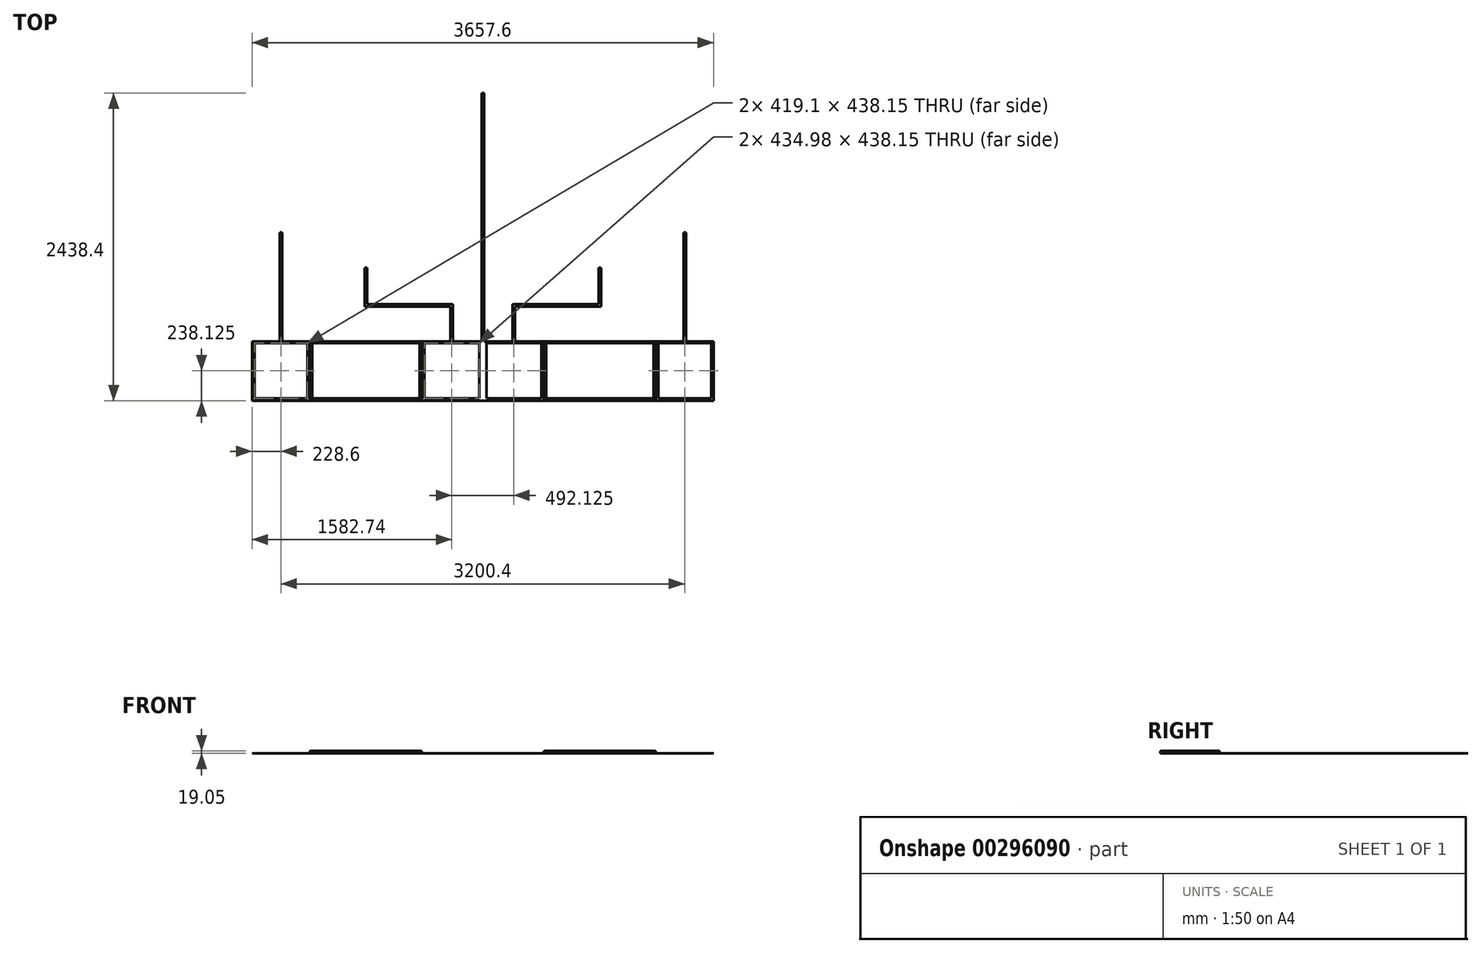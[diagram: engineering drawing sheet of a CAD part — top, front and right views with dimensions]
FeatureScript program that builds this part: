
annotation { "Feature Type Name" : "Feature", "Feature Type Description" : "" }
export const myFeature = defineFeature(function(context is Context, id is Id, definition is map)
    precondition{}
    {
        {
            var Q0;
            Q0=qCreatedBy(makeId("Top.planeOp"),FACE);
            var sketch = newSketch(context, id + "F0", { "sketchPlane" : qUnion([Q0])});
            skLineSegment(sketch, "E0.bottom", {"start": v(0, 1187.45) * mm, "end": v(-1828.8, 1187.45) * mm});
            skLineSegment(sketch, "E0.top", {"start": v(0, -1250.95) * mm, "end": v(-1828.8, -1250.95) * mm});
            skLineSegment(sketch, "E0.right", {"start": v(-1828.8, 1187.45) * mm, "end": v(-1828.8, -1250.95) * mm});
            skPoint(sketch, "E0.middle", {"position": v(0, 0) * mm});
            skLineSegment(sketch, "E1.bottom", {"start": v(0, 1187.45) * mm, "end": v(-9.52, 1187.45) * mm});
            skLineSegment(sketch, "E1.top", {"start": v(0, -1250.95) * mm, "end": v(-9.52, -1250.95) * mm});
            skLineSegment(sketch, "E1.right", {"start": v(-9.53, 1187.45) * mm, "end": v(-9.53, -1250.95) * mm});
            skPoint(sketch, "E2", {"position": v(-1828.8, -793.75) * mm});
            skLineSegment(sketch, "E3", {"start": v(-1809.75, -793.75) * mm, "end": v(-1590.67, -793.75) * mm});
            skPoint(sketch, "E4", {"position": v(-1809.75, -1250.95) * mm});
            skLineSegment(sketch, "E5", {"start": v(-1809.75, -1231.9) * mm, "end": v(-1809.75, -793.75) * mm});
            skPoint(sketch, "E6", {"position": v(-1371.6, -1250.95) * mm});
            skPoint(sketch, "E7", {"position": v(-1390.65, -1250.95) * mm});
            skLineSegment(sketch, "E8", {"start": v(-1371.6, -1250.95) * mm, "end": v(-1371.6, -793.75) * mm});
            skLineSegment(sketch, "E9", {"start": v(-1390.65, -1231.9) * mm, "end": v(-1390.65, -793.75) * mm});
            skLineSegment(sketch, "E10.trimOffspring", {"start": v(-1390.65, -781.05) * mm, "end": v(-1809.75, -781.05) * mm});
            skPoint(sketch, "E11", {"position": v(-1828.8, -1231.9) * mm});
            skLineSegment(sketch, "E12", {"start": v(-1809.75, -1231.9) * mm, "end": v(-1390.65, -1231.9) * mm});
            skPoint(sketch, "E13", {"position": v(-482.6, -1250.95) * mm});
            skPoint(sketch, "E14", {"position": v(-501.65, -1250.95) * mm});
            skPoint(sketch, "E15", {"position": v(-1352.55, -1250.95) * mm});
            skLineSegment(sketch, "E16", {"start": v(-1352.55, -1231.9) * mm, "end": v(-1352.55, -793.75) * mm});
            skLineSegment(sketch, "E17", {"start": v(-482.6, -1250.95) * mm, "end": v(-482.6, -781.05) * mm});
            skLineSegment(sketch, "E18", {"start": v(-482.6, -793.75) * mm, "end": v(-482.6, -781.05) * mm});
            skLineSegment(sketch, "E19", {"start": v(-501.65, -1231.9) * mm, "end": v(-501.65, -793.75) * mm});
            skLineSegment(sketch, "E20", {"start": v(-1352.55, -1231.9) * mm, "end": v(-501.65, -1231.9) * mm});
            skLineSegment(sketch, "E21.trimOffspring", {"start": v(-501.65, -781.05) * mm, "end": v(-1352.55, -781.05) * mm});
            skPoint(sketch, "E22", {"position": v(-463.55, -1250.95) * mm});
            skPoint(sketch, "E23", {"position": v(-28.57, -1250.95) * mm});
            skLineSegment(sketch, "E24", {"start": v(-463.55, -1231.9) * mm, "end": v(-463.55, -793.75) * mm});
            skLineSegment(sketch, "E25", {"start": v(-28.58, -1231.9) * mm, "end": v(-28.58, -793.75) * mm});
            skLineSegment(sketch, "E26", {"start": v(-463.55, -1231.9) * mm, "end": v(-28.57, -1231.9) * mm});
            skLineSegment(sketch, "E27.trimOffspring", {"start": v(-28.58, -781.05) * mm, "end": v(-463.55, -781.05) * mm});
            skPoint(sketch, "E28", {"position": v(-246.06, -793.75) * mm});
            skPoint(sketch, "E29", {"position": v(-9.52, -793.75) * mm});
            skPoint(sketch, "E30", {"position": v(-246.06, -628.65) * mm});
            skLineSegment(sketch, "E31.top", {"start": v(-236.54, -793.75) * mm, "end": v(-255.59, -793.75) * mm});
            skLineSegment(sketch, "E31.left", {"start": v(-236.54, -463.55) * mm, "end": v(-236.54, -781.05) * mm});
            skLineSegment(sketch, "E31.right", {"start": v(-255.59, -504.83) * mm, "end": v(-255.59, -781.05) * mm});
            skPoint(sketch, "E32", {"position": v(-927.1, -793.75) * mm});
            skLineSegment(sketch, "E33.bottom", {"start": v(-917.58, -485.78) * mm, "end": v(-236.54, -485.78) * mm});
            skLineSegment(sketch, "E33.top", {"start": v(-936.35, -504.83) * mm, "end": v(-255.59, -504.83) * mm});
            skPoint(sketch, "E33.middle", {"position": v(-586.44, -495.3) * mm});
            skPoint(sketch, "E34", {"position": v(-927.1, -350.84) * mm});
            skLineSegment(sketch, "E35.bottom", {"start": v(-917.58, -504.83) * mm, "end": v(-936.63, -504.83) * mm});
            skLineSegment(sketch, "E35.top", {"start": v(-917.58, -196.85) * mm, "end": v(-936.63, -196.85) * mm});
            skLineSegment(sketch, "E35.left", {"start": v(-917.58, -485.78) * mm, "end": v(-917.58, -196.85) * mm});
            skLineSegment(sketch, "E35.right", {"start": v(-936.63, -504.83) * mm, "end": v(-936.63, -196.85) * mm});
            skPoint(sketch, "E36.trimOffspring.end.orphan", {"position": v(-917.85, -196.85) * mm});
            skPoint(sketch, "E37", {"position": v(-1600.2, -793.75) * mm});
            skPoint(sketch, "E38", {"position": v(-1600.2, -355.6) * mm});
            skLineSegment(sketch, "E39.bottom", {"start": v(-1609.72, -793.75) * mm, "end": v(-1590.67, -793.75) * mm});
            skLineSegment(sketch, "E39.top", {"start": v(-1609.72, 82.55) * mm, "end": v(-1590.67, 82.55) * mm});
            skLineSegment(sketch, "E39.left", {"start": v(-1609.73, -781.05) * mm, "end": v(-1609.73, 82.55) * mm});
            skLineSegment(sketch, "E39.right", {"start": v(-1590.68, -781.05) * mm, "end": v(-1590.68, 82.55) * mm});
            skPoint(sketch, "E40.orphan", {"position": v(-1600.2, 82.55) * mm});
            skPoint(sketch, "E41", {"position": v(0, 1187.45) * mm});
            skLineSegment(sketch, "E42", {"start": v(0, 1187.45) * mm, "end": v(0, -1250.95) * mm});
            skLineSegment(sketch, "E43.MirrorCS", {"start": v(0, 1187.45) * mm, "end": v(9.52, 1187.45) * mm});
            skLineSegment(sketch, "E44.MirrorCS", {"start": v(0, -1250.95) * mm, "end": v(9.52, -1250.95) * mm});
            skLineSegment(sketch, "E45.MirrorCS", {"start": v(9.52, 1187.45) * mm, "end": v(9.53, -1250.95) * mm});
            skLineSegment(sketch, "E46.MirrorCS", {"start": v(-1809.75, -793.75) * mm, "end": v(-1390.65, -793.75) * mm});
            skLineSegment(sketch, "E47", {"start": v(-1809.75, -781.05) * mm, "end": v(-1828.8, -781.05) * mm});
            skLineSegment(sketch, "E48", {"start": v(-1390.65, -781.05) * mm, "end": v(-1352.55, -781.05) * mm});
            skLineSegment(sketch, "E49.trimOffspring", {"start": v(-1352.55, -793.75) * mm, "end": v(-501.65, -793.75) * mm});
            skLineSegment(sketch, "E50", {"start": v(-1371.6, -793.75) * mm, "end": v(-1371.6, -781.05) * mm});
            skLineSegment(sketch, "E51.trimOffspring", {"start": v(-1352.55, -793.75) * mm, "end": v(-927.1, -793.75) * mm});
            skLineSegment(sketch, "E52", {"start": v(-501.65, -781.05) * mm, "end": v(-463.55, -781.05) * mm});
            skLineSegment(sketch, "E53.trimOffspring", {"start": v(-463.55, -793.75) * mm, "end": v(-28.58, -793.75) * mm});
            skLineSegment(sketch, "E54", {"start": v(-28.58, -781.05) * mm, "end": v(-9.53, -781.05) * mm});
            skLineSegment(sketch, "E55.trimOffspring", {"start": v(-9.52, -793.75) * mm, "end": v(0, -793.75) * mm});
            skLineSegment(sketch, "E56.MirrorCS", {"start": v(0, 1187.45) * mm, "end": v(-9.53, 1187.45) * mm});
            skLineSegment(sketch, "E57.MirrorCS", {"start": v(9.52, -793.75) * mm, "end": v(0, -793.75) * mm});
            skLineSegment(sketch, "E58.MirrorCS", {"start": v(1809.75, -781.05) * mm, "end": v(1828.8, -781.05) * mm});
            skLineSegment(sketch, "E59.MirrorCS", {"start": v(28.57, -781.05) * mm, "end": v(9.52, -781.05) * mm});
            skLineSegment(sketch, "E60.MirrorCS", {"start": v(1371.6, -793.75) * mm, "end": v(1371.6, -781.05) * mm});
            skLineSegment(sketch, "E61.MirrorCS", {"start": v(482.6, -793.75) * mm, "end": v(482.6, -781.05) * mm});
            skLineSegment(sketch, "E62.MirrorCS", {"start": v(501.65, -781.05) * mm, "end": v(463.55, -781.05) * mm});
            skLineSegment(sketch, "E63.MirrorCS", {"start": v(1390.65, -781.05) * mm, "end": v(1352.55, -781.05) * mm});
            skLineSegment(sketch, "E64.MirrorCS", {"start": v(917.57, -504.83) * mm, "end": v(936.62, -504.83) * mm});
            skLineSegment(sketch, "E65.MirrorCS", {"start": v(1609.72, -793.75) * mm, "end": v(1590.67, -793.75) * mm});
            skLineSegment(sketch, "E66.MirrorCS", {"start": v(917.57, -196.85) * mm, "end": v(936.62, -196.85) * mm});
            skLineSegment(sketch, "E67.MirrorCS", {"start": v(236.54, -793.75) * mm, "end": v(255.59, -793.75) * mm});
            skLineSegment(sketch, "E68.MirrorCS", {"start": v(1609.72, 82.55) * mm, "end": v(1590.67, 82.55) * mm});
            skPoint(sketch, "E69.MirrorP", {"position": v(246.06, -628.65) * mm});
            skLineSegment(sketch, "E70.MirrorCS", {"start": v(28.57, -781.05) * mm, "end": v(463.55, -781.05) * mm});
            skLineSegment(sketch, "E71.MirrorCS", {"start": v(1352.55, -793.75) * mm, "end": v(927.1, -793.75) * mm});
            skLineSegment(sketch, "E72.MirrorCS", {"start": v(463.55, -793.75) * mm, "end": v(28.57, -793.75) * mm});
            skPoint(sketch, "E73.MirrorP", {"position": v(927.1, -350.84) * mm});
            skLineSegment(sketch, "E74.MirrorCS", {"start": v(0, -1250.95) * mm, "end": v(1828.8, -1250.95) * mm});
            skLineSegment(sketch, "E75.MirrorCS", {"start": v(0, 1187.45) * mm, "end": v(1828.8, 1187.45) * mm});
            skPoint(sketch, "E76.MirrorP", {"position": v(1600.2, -355.6) * mm});
            skLineSegment(sketch, "E77.MirrorCS", {"start": v(1371.6, -1250.95) * mm, "end": v(1371.6, -793.75) * mm});
            skPoint(sketch, "E78.MirrorP", {"position": v(9.52, -793.75) * mm});
            skLineSegment(sketch, "E79.MirrorCS", {"start": v(1809.75, -793.75) * mm, "end": v(1390.65, -793.75) * mm});
            skPoint(sketch, "E80.MirrorP", {"position": v(482.6, -1250.95) * mm});
            skLineSegment(sketch, "E81.MirrorCS", {"start": v(1809.75, -793.75) * mm, "end": v(1590.67, -793.75) * mm});
            skLineSegment(sketch, "E82.MirrorCS", {"start": v(501.65, -781.05) * mm, "end": v(1352.55, -781.05) * mm});
            skPoint(sketch, "E83.MirrorP", {"position": v(28.57, -1250.95) * mm});
            skPoint(sketch, "E84.MirrorP", {"position": v(1828.8, -793.75) * mm});
            skPoint(sketch, "E85.MirrorP", {"position": v(1371.6, -1250.95) * mm});
            skLineSegment(sketch, "E86.MirrorCS", {"start": v(1828.8, 1187.45) * mm, "end": v(1828.8, -1250.95) * mm});
            skLineSegment(sketch, "E87.MirrorCS", {"start": v(482.6, -1250.95) * mm, "end": v(482.6, -781.05) * mm});
            skLineSegment(sketch, "E88.MirrorCS", {"start": v(1590.67, -781.05) * mm, "end": v(1590.67, 82.55) * mm});
            skPoint(sketch, "E89.MirrorP", {"position": v(917.85, -196.85) * mm});
            skLineSegment(sketch, "E90.MirrorCS", {"start": v(255.59, -504.83) * mm, "end": v(255.59, -781.05) * mm});
            skLineSegment(sketch, "E91.MirrorCS", {"start": v(1352.55, -1231.9) * mm, "end": v(1352.55, -793.75) * mm});
            skLineSegment(sketch, "E92.MirrorCS", {"start": v(1352.55, -793.75) * mm, "end": v(501.65, -793.75) * mm});
            skPoint(sketch, "E93.MirrorP", {"position": v(1600.2, 82.55) * mm});
            skLineSegment(sketch, "E94.MirrorCS", {"start": v(1809.75, -1231.9) * mm, "end": v(1390.65, -1231.9) * mm});
            skLineSegment(sketch, "E95.MirrorCS", {"start": v(1390.65, -781.05) * mm, "end": v(1809.75, -781.05) * mm});
            skPoint(sketch, "E96.MirrorP", {"position": v(1828.8, -1231.9) * mm});
            skLineSegment(sketch, "E97.MirrorCS", {"start": v(936.62, -504.83) * mm, "end": v(936.62, -196.85) * mm});
            skLineSegment(sketch, "E98.MirrorCS", {"start": v(917.57, -485.78) * mm, "end": v(236.54, -485.78) * mm});
            skPoint(sketch, "E99.MirrorP", {"position": v(501.65, -1250.95) * mm});
            skPoint(sketch, "E100.MirrorP", {"position": v(1600.2, -793.75) * mm});
            skLineSegment(sketch, "E101.MirrorCS", {"start": v(917.57, -485.78) * mm, "end": v(917.57, -196.85) * mm});
            skLineSegment(sketch, "E102.MirrorCS", {"start": v(1809.75, -1231.9) * mm, "end": v(1809.75, -793.75) * mm});
            skLineSegment(sketch, "E103.MirrorCS", {"start": v(28.58, -1231.9) * mm, "end": v(28.57, -793.75) * mm});
            skPoint(sketch, "E104.MirrorP", {"position": v(586.44, -495.3) * mm});
            skPoint(sketch, "E105.MirrorP", {"position": v(1809.75, -1250.95) * mm});
            skLineSegment(sketch, "E106.MirrorCS", {"start": v(236.54, -463.55) * mm, "end": v(236.54, -781.05) * mm});
            skPoint(sketch, "E107.MirrorP", {"position": v(463.55, -1250.95) * mm});
            skPoint(sketch, "E108.MirrorP", {"position": v(1390.65, -1250.95) * mm});
            skLineSegment(sketch, "E109.MirrorCS", {"start": v(1390.65, -1231.9) * mm, "end": v(1390.65, -793.75) * mm});
            skPoint(sketch, "E110.MirrorP", {"position": v(246.06, -793.75) * mm});
            skPoint(sketch, "E111.MirrorP", {"position": v(1352.55, -1250.95) * mm});
            skPoint(sketch, "E112.MirrorP", {"position": v(927.1, -793.75) * mm});
            skLineSegment(sketch, "E113.MirrorCS", {"start": v(463.55, -1231.9) * mm, "end": v(28.57, -1231.9) * mm});
            skLineSegment(sketch, "E114.MirrorCS", {"start": v(501.65, -1231.9) * mm, "end": v(501.65, -793.75) * mm});
            skLineSegment(sketch, "E115.MirrorCS", {"start": v(936.35, -504.83) * mm, "end": v(255.59, -504.83) * mm});
            skLineSegment(sketch, "E116.MirrorCS", {"start": v(1352.55, -1231.9) * mm, "end": v(501.65, -1231.9) * mm});
            skLineSegment(sketch, "E117.MirrorCS", {"start": v(1609.72, -781.05) * mm, "end": v(1609.72, 82.55) * mm});
            skLineSegment(sketch, "E118.MirrorCS", {"start": v(463.55, -1231.9) * mm, "end": v(463.55, -793.75) * mm});
            skSolve(sketch);
        }
        {
            var Q0;
            Q0=makeQuery(id+"F0.imprint","IMPRINT",FACE,{"disambiguationData":[TD([[makeQuery(id+"F0.imprint","IMPRINT",EDGE,{"derivedFrom":sQuery(id+"F0.wireOp",EDGE,"E39.top")}),-1.0]])]});
            var Q1;
            Q1=makeQuery(id+"F0.imprint","IMPRINT",FACE,{"disambiguationData":[TD([[makeQuery(id+"F0.imprint","IMPRINT",EDGE,{"derivedFrom":sQuery(id+"F0.wireOp",EDGE,"E5")}),1.0]])]});
            var Q2;
            {var subQ4=sQuery(id+"F0.wireOp",EDGE,"E17");Q2=makeQuery(id+"F0.imprint","IMPRINT",FACE,{"disambiguationData":[TD([[makeQuery(id+"F0.imprint","IMPRINT",EDGE,{"derivedFrom":subQ4}),-1.0]])]});}
            var Q3;
            {var subQ2=sQuery(id+"F0.wireOp",EDGE,"E31.left");Q3=makeQuery(id+"F0.imprint","IMPRINT",FACE,{"disambiguationData":[TD([[makeQuery(id+"F0.imprint","IMPRINT",EDGE,{"derivedFrom":subQ2}),-1.0]])]});}
            var Q4;
            {var subQ0=sQuery(id+"F0.wireOp",EDGE,"E0.bottom");var subQ5=sQuery(id+"F0.wireOp",EDGE,"E1.right");var subQ6=makeQuery(id+"F0.imprint","INTERSECT",VERTEX,{"derivedFrom":[subQ0,subQ5]});Q4=makeQuery(id+"F0.imprint","IMPRINT",FACE,{"disambiguationData":[TD([[makeQuery(id+"F0.imprint","IMPRINT",EDGE,{"disambiguationData":[TD([[subQ6,-1.0]])],"derivedFrom":subQ5}),1.0]])]});}
            var Q5;
            {var subQ0=sQuery(id+"F0.wireOp",EDGE,"9973ab8d-1ef1-4f2a-91f5-c3c454b1e91057.MirrorCS");var subQ5=sQuery(id+"F0.wireOp",EDGE,"E45.MirrorCS");var subQ6=makeQuery(id+"F0.imprint","INTERSECT",VERTEX,{"derivedFrom":[subQ5,subQ0]});Q5=makeQuery(id+"F0.imprint","IMPRINT",FACE,{"disambiguationData":[TD([[makeQuery(id+"F0.imprint","IMPRINT",EDGE,{"disambiguationData":[TD([[subQ6,-1.0]])],"derivedFrom":subQ5}),-1.0]])]});}
            var Q6;
            {var subQ0=sQuery(id+"F0.wireOp",EDGE,"E0.top");var subQ5=sQuery(id+"F0.wireOp",EDGE,"E1.right");var subQ6=makeQuery(id+"F0.imprint","INTERSECT",VERTEX,{"derivedFrom":[subQ0,subQ5]});Q6=makeQuery(id+"F0.imprint","IMPRINT",FACE,{"disambiguationData":[TD([[makeQuery(id+"F0.imprint","IMPRINT",EDGE,{"disambiguationData":[TD([[subQ6,1.0]])],"derivedFrom":subQ5}),1.0]])]});}
            var Q7;
            {var subQ0=sQuery(id+"F0.wireOp",EDGE,"9973ab8d-1ef1-4f2a-91f5-c3c454b1e91069.MirrorCS");var subQ5=sQuery(id+"F0.wireOp",EDGE,"E45.MirrorCS");var subQ6=makeQuery(id+"F0.imprint","INTERSECT",VERTEX,{"derivedFrom":[subQ5,subQ0]});Q7=makeQuery(id+"F0.imprint","IMPRINT",FACE,{"disambiguationData":[TD([[makeQuery(id+"F0.imprint","IMPRINT",EDGE,{"disambiguationData":[TD([[subQ6,1.0]])],"derivedFrom":subQ5}),-1.0]])]});}
            var Q8;
            {var subQ5=sQuery(id+"F0.wireOp",EDGE,"9973ab8d-1ef1-4f2a-91f5-c3c454b1e9109.MirrorCS");Q8=makeQuery(id+"F0.imprint","IMPRINT",FACE,{"disambiguationData":[TD([[makeQuery(id+"F0.imprint","IMPRINT",EDGE,{"derivedFrom":subQ5}),1.0]])]});}
            var Q9;
            {var subQ4=sQuery(id+"F0.wireOp",EDGE,"9973ab8d-1ef1-4f2a-91f5-c3c454b1e9106.MirrorCS");Q9=makeQuery(id+"F0.imprint","IMPRINT",FACE,{"disambiguationData":[TD([[makeQuery(id+"F0.imprint","IMPRINT",EDGE,{"derivedFrom":subQ4}),1.0]])]});}
            var Q10;
            Q10=makeQuery(id+"F0.imprint","IMPRINT",FACE,{"disambiguationData":[TD([[makeQuery(id+"F0.imprint","IMPRINT",EDGE,{"derivedFrom":sQuery(id+"F0.wireOp",EDGE,"9973ab8d-1ef1-4f2a-91f5-c3c454b1e91013.MirrorCS")}),1.0]])]});
            var Q11;
            Q11=makeQuery(id+"F0.imprint","IMPRINT",FACE,{"disambiguationData":[TD([[makeQuery(id+"F0.imprint","IMPRINT",EDGE,{"derivedFrom":sQuery(id+"F0.wireOp",EDGE,"9973ab8d-1ef1-4f2a-91f5-c3c454b1e91011.MirrorCS")}),1.0]])]});
            extrude(context, id + "F1", {"entities" : qUnion([Q0, Q1, Q2, Q3, Q4, Q5, Q6, Q7, Q8, Q9, Q10, Q11]), "depth" : 0.25 * mm});
        }
        {
            var Q0;
            {var subQ2=sQuery(id+"F0.wireOp",EDGE,"E8");Q0=makeQuery(id+"F0.imprint","IMPRINT",FACE,{"disambiguationData":[TD([[makeQuery(id+"F0.imprint","IMPRINT",EDGE,{"derivedFrom":subQ2}),-1.0]])]});}
            var Q1;
            {var subQ3=sQuery(id+"F0.wireOp",EDGE,"9973ab8d-1ef1-4f2a-91f5-c3c454b1e9109.MirrorCS");Q1=makeQuery(id+"F0.imprint","IMPRINT",FACE,{"disambiguationData":[TD([[makeQuery(id+"F0.imprint","IMPRINT",EDGE,{"derivedFrom":subQ3}),-1.0]])]});}
            extrude(context, id + "F2", {"entities" : qUnion([Q0, Q1]), "depth" : 19.05 * mm});
        }
        {
            var Q0;
            Q0=makeQuery(id+"F2.opExtrude","CAP_FACE",FACE,{"disambiguationData":[OSD([sQuery(id+"F0.wireOp",EDGE,"E8"),sQuery(id+"F0.wireOp",EDGE,"E16"),sQuery(id+"F0.wireOp",EDGE,"E17"),sQuery(id+"F0.wireOp",EDGE,"E18"),sQuery(id+"F0.wireOp",EDGE,"E19"),sQuery(id+"F0.wireOp",EDGE,"E20"),sQuery(id+"F0.wireOp",EDGE,"E21.trimOffspring"),sQuery(id+"F0.wireOp",EDGE,"E0.top"),sQuery(id+"F0.wireOp",EDGE,"E46.MirrorCS")])],"isStart":false});
            fillet(context, id + "F3", {"entities" : qUnion([Q0]), "radius" : 9.52 * mm, "tangentPropagation" : true, "allowEdgeOverflow" : false});
        }
        {
            var Q0;
            {var subQ15=sQuery(id+"F0.wireOp",EDGE,"E59.MirrorCS");Q0=makeQuery(id+"F0.imprint","IMPRINT",FACE,{"disambiguationData":[TD([[makeQuery(id+"F0.imprint","IMPRINT",EDGE,{"derivedFrom":subQ15}),1.0]])]});}
            var Q1;
            {var subQ3=sQuery(id+"F0.wireOp",EDGE,"E57.MirrorCS");Q1=makeQuery(id+"F0.imprint","IMPRINT",FACE,{"disambiguationData":[TD([[makeQuery(id+"F0.imprint","IMPRINT",EDGE,{"derivedFrom":subQ3}),1.0]])]});}
            var Q2;
            {var subQ2=sQuery(id+"F0.wireOp",EDGE,"E55.trimOffspring");Q2=makeQuery(id+"F0.imprint","IMPRINT",FACE,{"disambiguationData":[TD([[makeQuery(id+"F0.imprint","IMPRINT",EDGE,{"derivedFrom":subQ2}),-1.0]])]});}
            var Q3;
            {var subQ4=sQuery(id+"F0.wireOp",EDGE,"E55.trimOffspring");Q3=makeQuery(id+"F0.imprint","IMPRINT",FACE,{"disambiguationData":[TD([[makeQuery(id+"F0.imprint","IMPRINT",EDGE,{"derivedFrom":subQ4}),1.0]])]});}
            var Q4;
            {var subQ4=sQuery(id+"F0.wireOp",EDGE,"E57.MirrorCS");Q4=makeQuery(id+"F0.imprint","IMPRINT",FACE,{"disambiguationData":[TD([[makeQuery(id+"F0.imprint","IMPRINT",EDGE,{"derivedFrom":subQ4}),-1.0]])]});}
            var Q5;
            {var subQ6=sQuery(id+"F0.wireOp",EDGE,"E64.MirrorCS");Q5=makeQuery(id+"F0.imprint","IMPRINT",FACE,{"disambiguationData":[TD([[makeQuery(id+"F0.imprint","IMPRINT",EDGE,{"derivedFrom":subQ6}),1.0]])]});}
            var Q6;
            Q6=makeQuery(id+"F0.imprint","IMPRINT",FACE,{"disambiguationData":[TD([[makeQuery(id+"F0.imprint","IMPRINT",EDGE,{"derivedFrom":sQuery(id+"F0.wireOp",EDGE,"E68.MirrorCS")}),1.0]])]});
            var Q7;
            {var subQ4=sQuery(id+"F0.wireOp",EDGE,"E58.MirrorCS");Q7=makeQuery(id+"F0.imprint","IMPRINT",FACE,{"disambiguationData":[TD([[makeQuery(id+"F0.imprint","IMPRINT",EDGE,{"derivedFrom":subQ4}),-1.0]])]});}
            extrude(context, id + "F4", {"entities" : qUnion([Q0, Q1, Q2, Q3, Q4, Q5, Q6, Q7]), "operationType" : NewBodyOperationType.ADD, "depth" : 0.25 * mm});
        }
        {
            var Q0;
            {var subQ10=sQuery(id+"F0.wireOp",EDGE,"E60.MirrorCS");Q0=makeQuery(id+"F0.imprint","IMPRINT",FACE,{"disambiguationData":[TD([[makeQuery(id+"F0.imprint","IMPRINT",EDGE,{"derivedFrom":subQ10}),1.0]])]});}
            extrude(context, id + "F5", {"entities" : qUnion([Q0]), "depth" : 19.05 * mm});
        }
        {
            var Q0;
            Q0=makeQuery(id+"F5.opExtrude","CAP_FACE",FACE,{"disambiguationData":[OSD([sQuery(id+"F0.wireOp",EDGE,"E60.MirrorCS"),sQuery(id+"F0.wireOp",EDGE,"E62.MirrorCS"),sQuery(id+"F0.wireOp",EDGE,"E63.MirrorCS"),sQuery(id+"F0.wireOp",EDGE,"E77.MirrorCS"),sQuery(id+"F0.wireOp",EDGE,"E82.MirrorCS"),sQuery(id+"F0.wireOp",EDGE,"E87.MirrorCS"),sQuery(id+"F0.wireOp",EDGE,"E74.MirrorCS"),sQuery(id+"F0.wireOp",EDGE,"E91.MirrorCS"),sQuery(id+"F0.wireOp",EDGE,"E92.MirrorCS"),sQuery(id+"F0.wireOp",EDGE,"E114.MirrorCS"),sQuery(id+"F0.wireOp",EDGE,"E116.MirrorCS")])],"isStart":false});
            fillet(context, id + "F6", {"entities" : qUnion([Q0]), "radius" : 9.52 * mm, "tangentPropagation" : true, "allowEdgeOverflow" : false});
        }
    });
